# Revit family: dotoo_spot_-_dse_2000_840_00806087_de06
name_source: partatom
category: Lighting Fixtures
units: mm (PartAtom-declared; Revit-internal decimal feet)

## family parameters
Cut with Voids When Loaded = No
Host = Face
Light Source = No
Part Type = Normal
Room Calculation Point = No
Round Connector Dimension = Use Diameter
Shared = No

## types (1)
- DOTOO.spot - DSE 2000/840 (1 x LED, 2100 lm, 4000K)
    Apparent Load = 20 VA
    Approval mark = CE
    CIE Flux Codes = 83 98 100 100 100
    Color Rendering = 80-89
    Color Temperature = 4000K
    Control Gear = Electronic ballast
    Default Elevation = 1800 mm
    Description = DSE 2000/840|Recessed luminaire|light source: LED|work equipment: Electronic ballast|connected load: 220-240 V, 50/60 Hz|Power consumption: approx. 20 W|standby: approx. 0,20|power factor: approx. 0,900|luminous flux: 2100 lm|luminous efficacy: 105 lm/W|light distribution: Direct|direct ratio: approx. 100 %|colour temperature: Cold white, ca. 4000 K|color rendering index (CRI): >= 80|chromaticity tolerance:  3 SDCM|System of protection: IP 20|class of protection: II|technology: Switchable|operation: External|luminaire body|material: Sheet metal|colour: White|weight (net): approx. 0.9 kg|mains lead: 0.35 m Connector|Fastening: Tension spring|glare control: Prism aperture|luminance(L65): <= 3300 cd/m|unified glare rating(4H 8H): <=  19|special features: Flicker-free, Low installation depth thanks to external ballast, Suitable as emergency lighting, Ceiling installation without tools by means of tension springs, Strain relief with the possibility of through-wiring, As supplement for room depths and walking areas|
    Height = 0 mm  [stored 0 ft]
    Lamp = 1 x LED
    Lamp Light Flux = 2100 lm
    Lamp count = 1
    Length = 216 mm
    Luminous efficacy = 105 lm/W
    Manufacturer = Waldmann
    ModVariant = No
    Model = 00806087
    Mounting Place = Ceiling
    Mounting Type = Recessed
    Number of Poles = 1
    OnlyDefault = Yes
    Power Factor = 1
    Product Name = DOTOO.spot - DSE 2000/840
    Product group = Recessed luminaire
    ProductGroupID = 4
    Protection Class = Protection class II
    Protection Degree = IP 20
    RLX_Detail_Level = 1
    RLX_Emergency_Light_Flux = 0 lm
    RLX_Emergency_Type = 0
    RLX_Emergency_Type_DB = No
    RlxData = <blob elided: 73229 chars, md5=f77b14d3>
    Socket = socket
    Standby Power = 0 W
    System Light Flux = 2100 lm
    System Power = 20 W
    Type Comments = Product without accessories
    Type Image = 114276000-00806088.jpg
    URL = http://relux.com
    VarID = ---
    Voltage = 230 V
    Voltage Range = 220-240 V
    Weight = 0.00 kg
    Width = 0 mm  [stored 0 ft]

note: [stored X ft] marks values corroborated as IEEE doubles in the binary element streams (Revit-internal decimal feet)

## geometry (parser evidence)
native form markers: Sweep x9
no freeform markers — native parametric forms only
